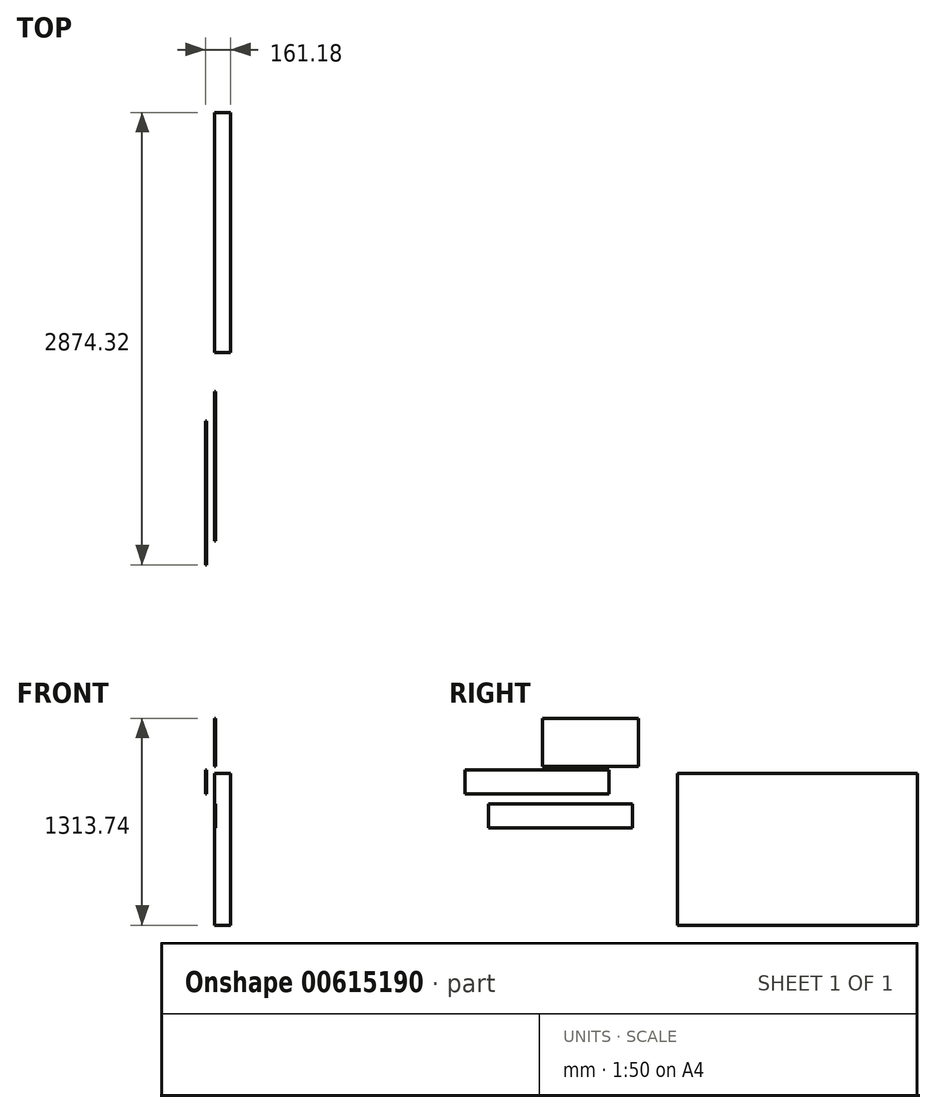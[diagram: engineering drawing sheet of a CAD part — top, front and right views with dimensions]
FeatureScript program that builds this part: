
annotation { "Feature Type Name" : "Feature", "Feature Type Description" : "" }
export const myFeature = defineFeature(function(context is Context, id is Id, definition is map)
    precondition{}
    {
        {
            var Q0;
            Q0=qCreatedBy(makeId("Front.planeOp"),FACE);
            var sketch = newSketch(context, id + "F0", { "sketchPlane" : qUnion([Q0])});
            skLineSegment(sketch, "E0.bottom", {"start": v(-59.58, 130.1) * mm, "end": v(-53.23, 130.1) * mm});
            skLineSegment(sketch, "E0.top", {"start": v(-59.58, -22.3) * mm, "end": v(-53.23, -22.3) * mm});
            skLineSegment(sketch, "E0.left", {"start": v(-59.58, 130.1) * mm, "end": v(-59.58, -22.3) * mm});
            skLineSegment(sketch, "E0.right", {"start": v(-53.23, 130.1) * mm, "end": v(-53.23, -22.3) * mm});
            skSolve(sketch);
        }
        {
            var Q0;
            Q0=makeQuery(id+"F0.imprint","IMPRINT",FACE,{"disambiguationData":[TD([[makeQuery(id+"F0.imprint","IMPRINT",EDGE,{"derivedFrom":sQuery(id+"F0.wireOp",EDGE,"E0.bottom")}),-1.0]])]});
            extrude(context, id + "F1", {"entities" : qUnion([Q0]), "depth" : 914.4 * mm, "offsetDistance" : 25.4 * mm});
        }
        {
            var Q0;
            Q0=qCreatedBy(makeId("Right.planeOp"),FACE);
            var sketch = newSketch(context, id + "F2", { "sketchPlane" : qUnion([Q0])});
            skLineSegment(sketch, "E1.bottom", {"start": v(-762.5, -87.55) * mm, "end": v(151.9, -87.55) * mm});
            skLineSegment(sketch, "E1.top", {"start": v(-762.5, -239.95) * mm, "end": v(151.9, -239.95) * mm});
            skLineSegment(sketch, "E1.left", {"start": v(-762.5, -87.55) * mm, "end": v(-762.5, -239.95) * mm});
            skLineSegment(sketch, "E1.right", {"start": v(151.9, -87.55) * mm, "end": v(151.9, -239.95) * mm});
            skSolve(sketch);
        }
        {
            var Q0;
            Q0=makeQuery(id+"F2.imprint","IMPRINT",FACE,{"disambiguationData":[TD([[makeQuery(id+"F2.imprint","IMPRINT",EDGE,{"derivedFrom":sQuery(id+"F2.wireOp",EDGE,"E1.bottom")}),-1.0]])]});
            extrude(context, id + "F3", {"entities" : qUnion([Q0]), "depth" : 6.35 * mm, "offsetDistance" : 25.4 * mm});
        }
        {
            var Q0;
            Q0=qCreatedBy(makeId("Right.planeOp"),FACE);
            var sketch = newSketch(context, id + "F4", { "sketchPlane" : qUnion([Q0])});
            skLineSegment(sketch, "E2.bottom", {"start": v(-421.45, 152.26) * mm, "end": v(188.15, 152.26) * mm});
            skLineSegment(sketch, "E2.top", {"start": v(-421.45, 457.06) * mm, "end": v(188.15, 457.06) * mm});
            skLineSegment(sketch, "E2.left", {"start": v(-421.45, 152.26) * mm, "end": v(-421.45, 457.06) * mm});
            skLineSegment(sketch, "E2.right", {"start": v(188.15, 152.26) * mm, "end": v(188.15, 457.06) * mm});
            skSolve(sketch);
        }
        {
            var Q0;
            Q0=makeQuery(id+"F4.imprint","IMPRINT",FACE,{"disambiguationData":[TD([[makeQuery(id+"F4.imprint","IMPRINT",EDGE,{"derivedFrom":sQuery(id+"F4.wireOp",EDGE,"E2.bottom")}),1.0]])]});
            extrude(context, id + "F5", {"entities" : qUnion([Q0]), "depth" : 6.35 * mm, "offsetDistance" : 25.4 * mm});
        }
        {
            var Q0;
            Q0=qCreatedBy(makeId("Right.planeOp"),FACE);
            var sketch = newSketch(context, id + "F6", { "sketchPlane" : qUnion([Q0])});
            skLineSegment(sketch, "E3.bottom", {"start": v(435.92, -856.68) * mm, "end": v(1959.92, -856.68) * mm});
            skLineSegment(sketch, "E3.top", {"start": v(435.92, 108.52) * mm, "end": v(1959.92, 108.52) * mm});
            skLineSegment(sketch, "E3.left", {"start": v(435.92, -856.68) * mm, "end": v(435.92, 108.52) * mm});
            skLineSegment(sketch, "E3.right", {"start": v(1959.92, -856.68) * mm, "end": v(1959.92, 108.52) * mm});
            skSolve(sketch);
        }
        {
            var Q0;
            Q0=makeQuery(id+"F6.imprint","IMPRINT",FACE,{"disambiguationData":[TD([[makeQuery(id+"F6.imprint","IMPRINT",EDGE,{"derivedFrom":sQuery(id+"F6.wireOp",EDGE,"E3.bottom")}),1.0]])]});
            extrude(context, id + "F7", {"entities" : qUnion([Q0]), "depth" : 101.6 * mm, "offsetDistance" : 25.4 * mm});
        }
    });
